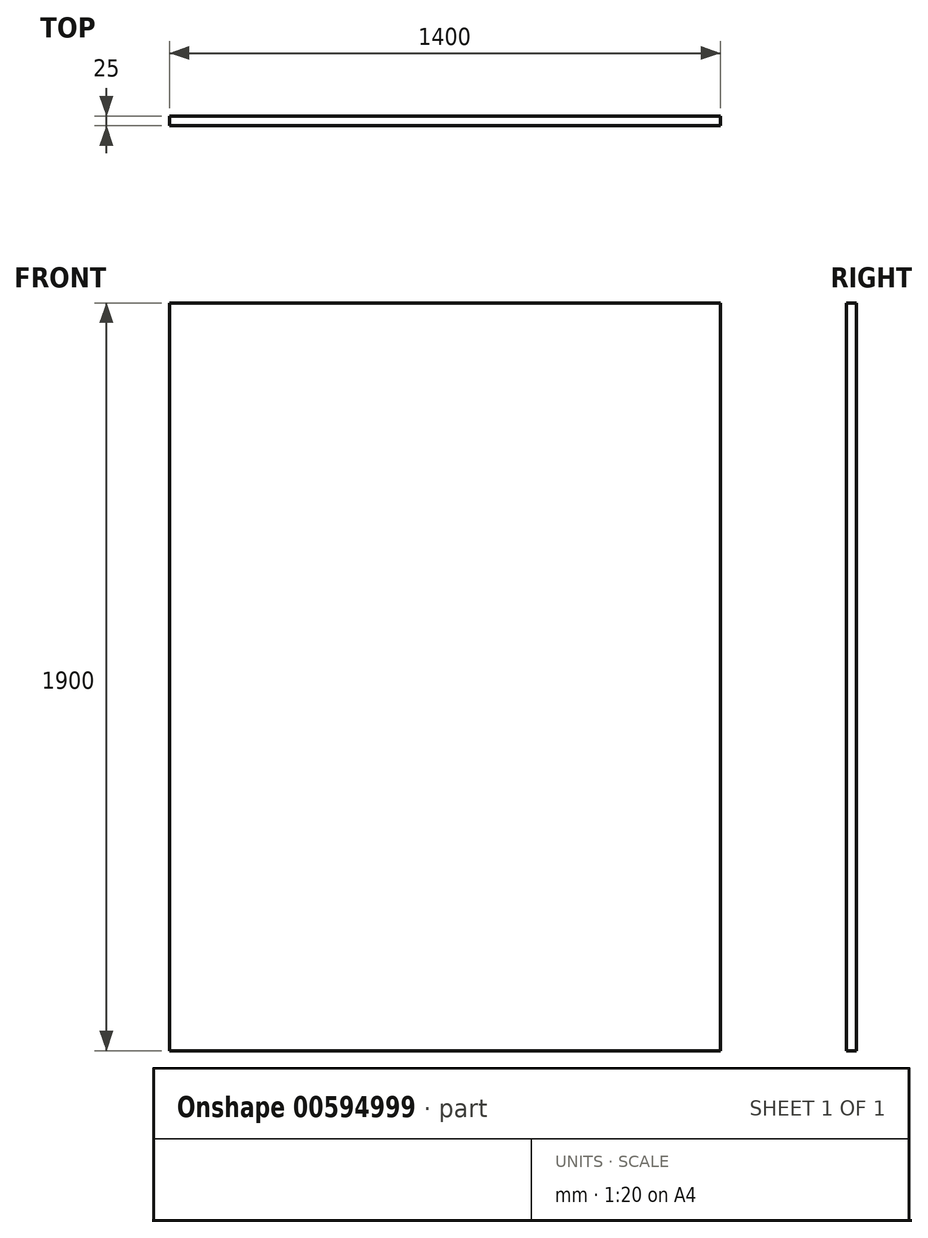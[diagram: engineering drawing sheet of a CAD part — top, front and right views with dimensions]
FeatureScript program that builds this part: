
annotation { "Feature Type Name" : "Feature", "Feature Type Description" : "" }
export const myFeature = defineFeature(function(context is Context, id is Id, definition is map)
    precondition{}
    {
        {
            var Q0;
            Q0=qCreatedBy(makeId("Front.planeOp"),FACE);
            var sketch = newSketch(context, id + "F0", { "sketchPlane" : qUnion([Q0])});
            skLineSegment(sketch, "E0.bottom", {"start": v(0, 0) * mm, "end": v(1400, 0) * mm});
            skLineSegment(sketch, "E0.top", {"start": v(0, 1900) * mm, "end": v(1400, 1900) * mm});
            skLineSegment(sketch, "E0.left", {"start": v(0, 0) * mm, "end": v(0, 1900) * mm});
            skLineSegment(sketch, "E0.right", {"start": v(1400, 0) * mm, "end": v(1400, 1900) * mm});
            skSolve(sketch);
        }
        {
            var Q0;
            Q0 = qSketchRegion(id + "F0", true);
            extrude(context, id + "F1", {"entities" : qUnion([Q0]), "depth" : 25 * mm, "offsetDistance" : 25 * mm});
        }
    });
